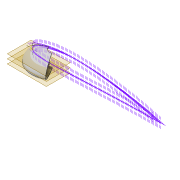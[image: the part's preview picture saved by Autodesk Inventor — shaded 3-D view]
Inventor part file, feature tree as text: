
AUTODESK INVENTOR PART (.ipt)
format: ipt  version: 2022 (Build 260153000, 153)  size: 536,064 bytes
history: native  units: mm
features: sketch x6, extrude x5, plane x3, thicken_offset x2, projected_geometry x2, shell x1, revolve x1, fillet x1
ambient origin geometry x8: Origin, YZ Plane, XZ Plane, XY Plane, X Axis, Y Axis, Z Axis, Center Point
bodies: Solid1 (feature_tree)
feature tree (21):
  extrude  "Extrusion1"  Depth=1.0mm
  shell  "Shell1"  Thickness=80.0mm
  extrude  "Extrusion16"  TaperAngle=120.0deg  [1 undecoded]
  revolve  "Revolution2"  [1 undecoded]
  extrude  "Extrusion17"  Depth=100.0mm TaperAngle=0.0deg
  plane  "Work Plane4"
  plane  "Work Plane5"
  plane  "Work Plane6"
  sketch  "Sketch41"  dims[d176=36.0mm d179=4.0mm]
  thicken_offset  "Thicken1"
  thicken_offset  "Thicken2"
  extrude  "Extrusion18"  Depth=4.0mm
  extrude  "Extrusion21"  Depth=2.2mm
  fillet  "Fillet5"  Radius=1.2mm
  sketch  "Sketch3"  dims[d0=1.0mm d1=0.0mm d2=1.0mm d159=80.0mm]
  sketch  "Sketch37"  dims[d160=10.0mm d161=0.0mm d163=120.0deg]
  sketch  "Sketch39"  dims[d164=1.0mm d165=0.0mm d166=6.454mm d167=16.2mm d168=-16.2mm]
  projected_geometry  "Projected Loop21"
  sketch  "Sketch40"  dims[d169=33.2mm d170=100.0mm d171=0.0mm]
  projected_geometry  "Projected Loop22"
  sketch  "Sketch43"  dims[d180=5.3mm d181=0.0mm d182=2.2mm d183=1.2mm d184=1.2mm d185=1.2mm d186=1.5mm]
note: 2 required parameter values undecoded (feature->parameter linkage not recoverable at this tier; creation-order binding heuristic only, values carry confidence <= 0.55)